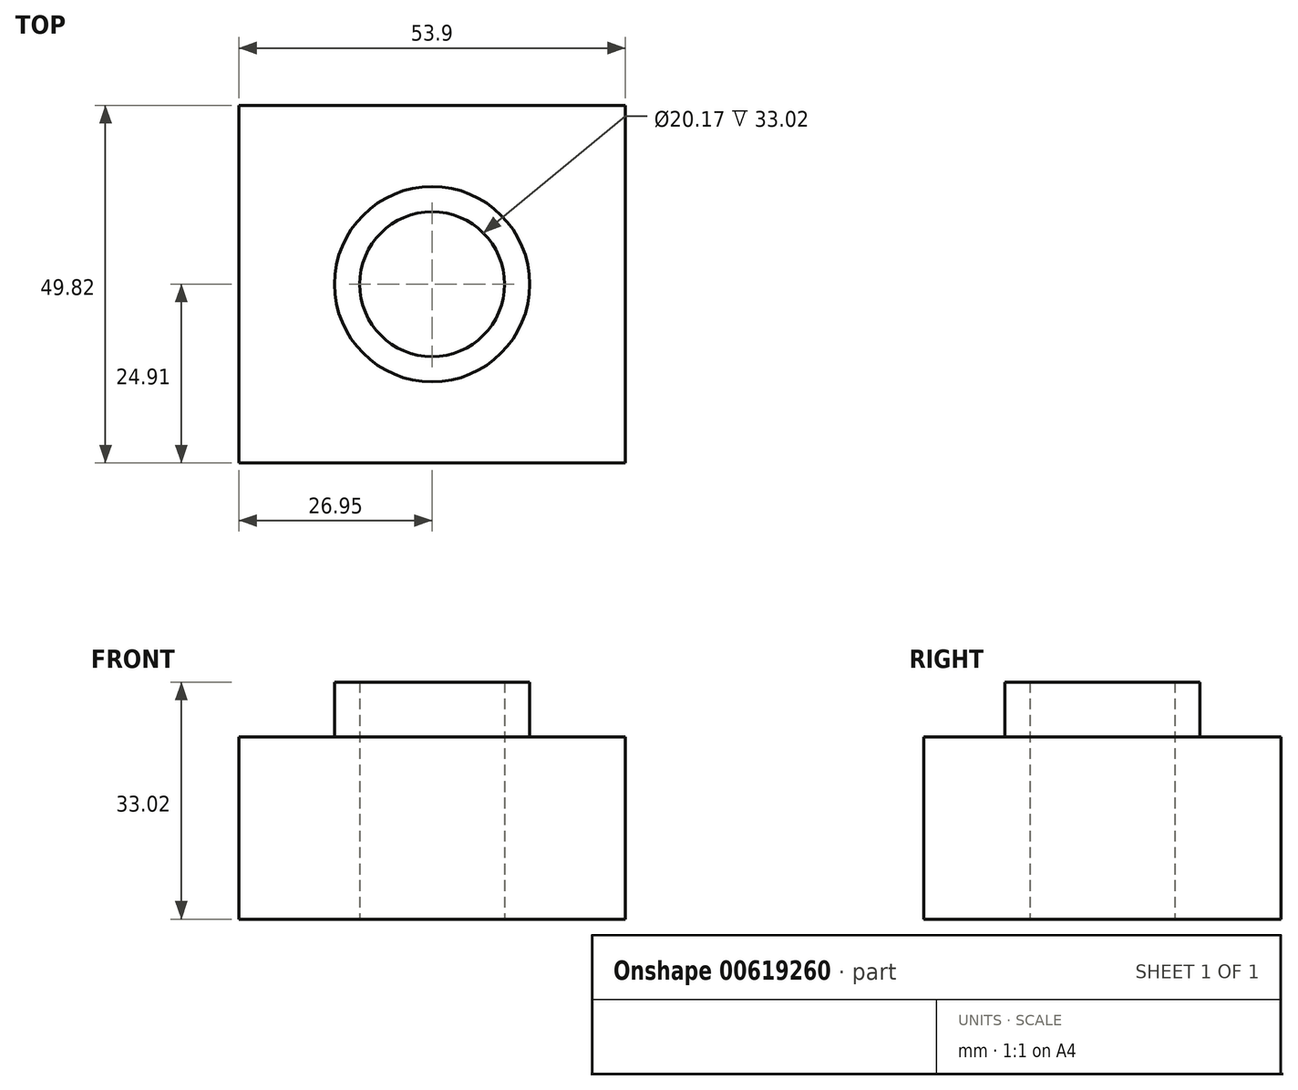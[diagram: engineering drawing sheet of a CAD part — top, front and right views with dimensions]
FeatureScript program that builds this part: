
annotation { "Feature Type Name" : "Feature", "Feature Type Description" : "" }
export const myFeature = defineFeature(function(context is Context, id is Id, definition is map)
    precondition{}
    {
        {
            var Q0;
            Q0=qCreatedBy(makeId("Top.planeOp"),FACE);
            var sketch = newSketch(context, id + "F0", { "sketchPlane" : qUnion([Q0])});
            skLineSegment(sketch, "E0.bottom", {"start": v(26.95, -24.91) * mm, "end": v(-26.95, -24.91) * mm});
            skLineSegment(sketch, "E0.top", {"start": v(26.95, 24.91) * mm, "end": v(-26.95, 24.91) * mm});
            skLineSegment(sketch, "E0.left", {"start": v(26.95, -24.91) * mm, "end": v(26.95, 24.91) * mm});
            skLineSegment(sketch, "E0.right", {"start": v(-26.95, -24.91) * mm, "end": v(-26.95, 24.91) * mm});
            skPoint(sketch, "E0.middle", {"position": v(0, 0) * mm});
            skCircle(sketch, "E1", {"center": v(0, 0) * mm, "radius": 13.6 * mm});
            skCircle(sketch, "E2", {"center": v(0, 0) * mm, "radius": 10.08 * mm});
            skSolve(sketch);
        }
        {
            var Q0;
            Q0=makeQuery(id+"F0.imprint","IMPRINT",FACE,{"disambiguationData":[TD([[makeQuery(id+"F0.imprint","IMPRINT",EDGE,{"derivedFrom":sQuery(id+"F0.wireOp",EDGE,"E0.bottom")}),-1.0]])]});
            extrude(context, id + "F1", {"entities" : qUnion([Q0]), "depth" : 25.4 * mm, "offsetDistance" : 25.4 * mm});
        }
        {
            var Q0;
            Q0=makeQuery(id+"F0.imprint","IMPRINT",FACE,{"disambiguationData":[TD([[makeQuery(id+"F0.imprint","IMPRINT",EDGE,{"derivedFrom":sQuery(id+"F0.wireOp",EDGE,"E1")}),1.0]])]});
            extrude(context, id + "F2", {"entities" : qUnion([Q0]), "operationType" : NewBodyOperationType.ADD, "depth" : 33.02 * mm, "offsetDistance" : 25.4 * mm});
        }
    });
